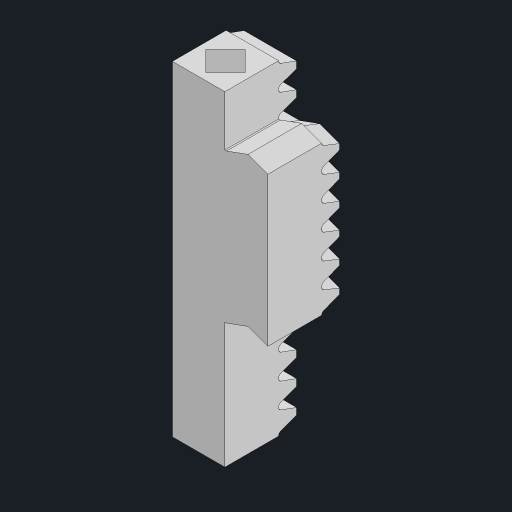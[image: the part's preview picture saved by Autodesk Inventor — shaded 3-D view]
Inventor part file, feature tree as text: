
AUTODESK INVENTOR PART (.ipt)
format: ipt  version: 2023.2 (Build 272271030, 271C)  size: 682,496 bytes
history: native  units: mm
features: sketch x6, projected_geometry x5, extrude x4, sweep x1, pattern_linear x1
ambient origin geometry x8: Origin, YZ Plane, XZ Plane, XY Plane, X Axis, Y Axis, Z Axis, Center Point
bodies: Solid1 (feature_tree)
feature tree (17):
  extrude  "Extrusion1"  Depth=40.840704mm
  sweep  "Sweep1"
  pattern_linear  "Rectangular Pattern1"  Spacing1=7.0mm  [1 undecoded]
  sketch  "Sketch4"  dims[d6=1.570796mm]
  extrude  "Extrusion7"  Depth=3.5mm
  extrude  "Extrusion8"  Depth=3.5mm
  extrude  "Extrusion9"  TaperAngle=0.0deg  [1 undecoded]
  sketch  "Sketch1"  dims[d0=12.0mm d1=40.840704mm]
  sketch  "Sketch2"  dims[d2=9.0mm d3=0.0mm d4=1.0mm]
  projected_geometry  "Projected Loop1"
  sketch  "Sketch3"  dims[d5=1.25mm]
  projected_geometry  "Projected Loop2"
  sketch  "Sketch8"  dims[d7=12.217305mm]
  projected_geometry  "Projected Loop21"
  sketch  "Sketch9"  dims[d17=0.38mm d27=7.0mm d28=5.0mm d29=3.490659mm d30=0.0mm d31=0.0mm d32=140.0mm d34=3.141593mm d49=10.0mm d50=0.0mm d56=0.0mm d57=0.0mm d58=0.0mm d59=0.0mm d60=3.5mm d61=3.3mm d43=0.5mm d44=0.872665mm d45=0.5mm d46=0.872665mm]
  projected_geometry  "Projected Loop22"
  projected_geometry  "Projected Loop23"
note: 2 required parameter values undecoded (feature->parameter linkage not recoverable at this tier; creation-order binding heuristic only, values carry confidence <= 0.55)
